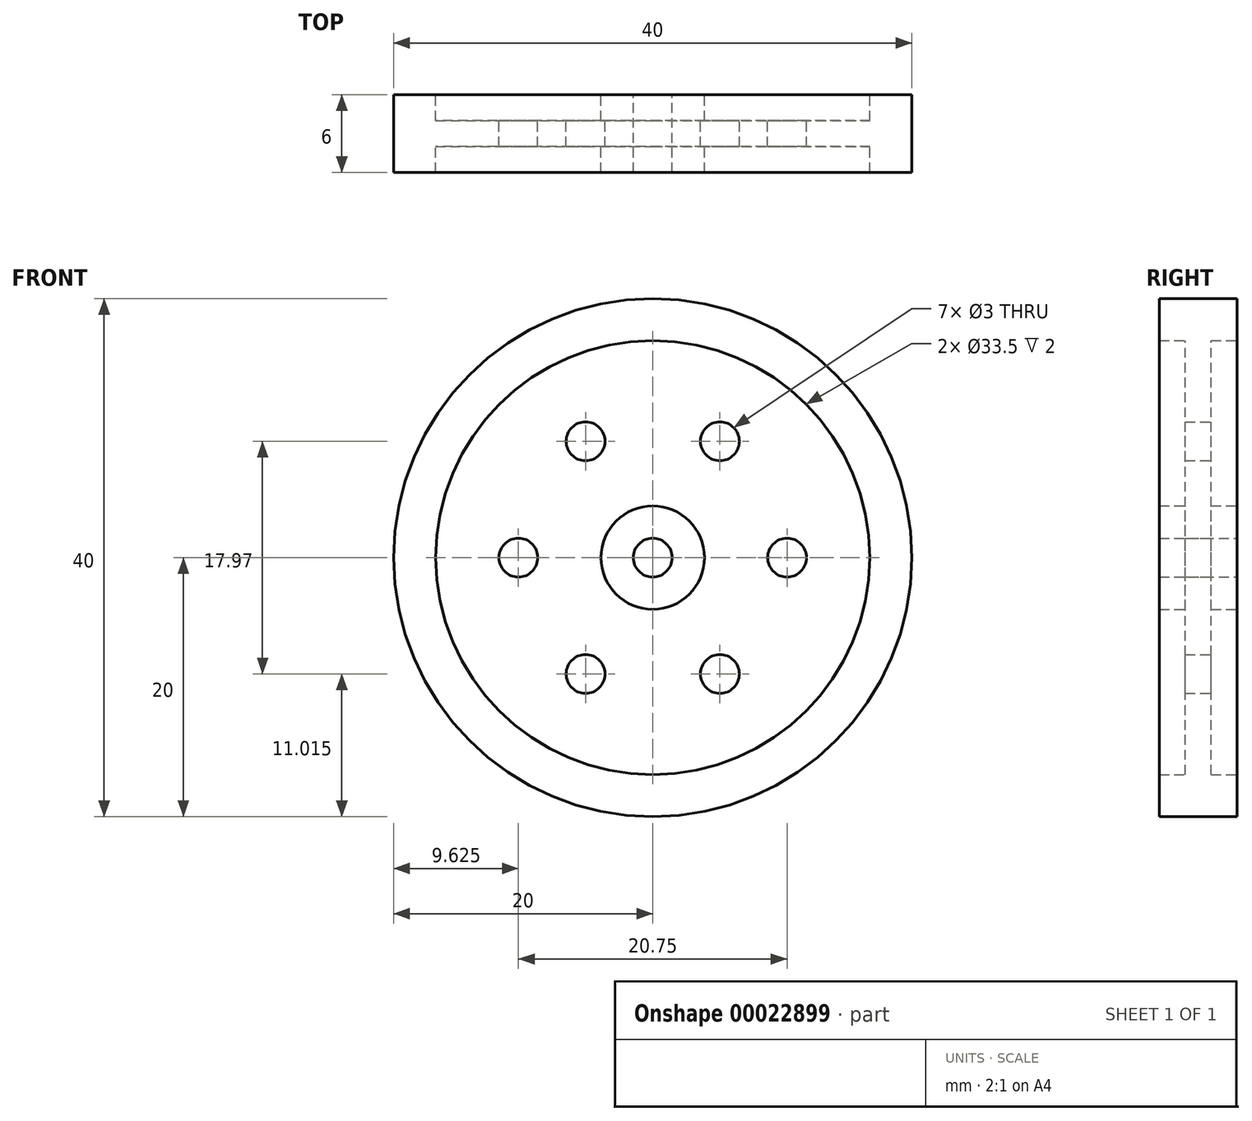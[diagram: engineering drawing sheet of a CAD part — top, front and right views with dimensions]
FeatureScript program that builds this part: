
annotation { "Feature Type Name" : "Feature", "Feature Type Description" : "" }
export const myFeature = defineFeature(function(context is Context, id is Id, definition is map)
    precondition{}
    {
        {
            var Q0;
            Q0=qCreatedBy(makeId("Front.planeOp"),FACE);
            var sketch = newSketch(context, id + "F0", { "sketchPlane" : qUnion([Q0])});
            skCircle(sketch, "E0", {"center": v(0, 0) * mm, "radius": 20 * mm});
            skCircle(sketch, "E1", {"center": v(0, 0) * mm, "radius": 16.75 * mm});
            skCircle(sketch, "E2", {"center": v(0, 0) * mm, "radius": 4 * mm});
            skCircle(sketch, "E3", {"center": v(0, 0) * mm, "radius": 1.5 * mm});
            skCircle(sketch, "E4", {"center": v(-10.38, 0) * mm, "radius": 1.5 * mm});
            skCircle(sketch, "E5.1.0", {"center": v(-5.19, -8.99) * mm, "radius": 1.5 * mm});
            skCircle(sketch, "E5.2.0", {"center": v(5.19, -8.99) * mm, "radius": 1.5 * mm});
            skCircle(sketch, "E5.3.0", {"center": v(10.38, 0) * mm, "radius": 1.5 * mm});
            skCircle(sketch, "E5.4.0", {"center": v(5.19, 8.99) * mm, "radius": 1.5 * mm});
            skCircle(sketch, "E5.5.0", {"center": v(-5.19, 8.99) * mm, "radius": 1.5 * mm});
            skSolve(sketch);
        }
        {
            var Q0;
            Q0=makeQuery(id+"F0.imprint","IMPRINT",FACE,{"disambiguationData":[TD([[makeQuery(id+"F0.imprint","IMPRINT",EDGE,{"derivedFrom":sQuery(id+"F0.wireOp",EDGE,"E1")}),1.0]])]});
            extrude(context, id + "F1", {"entities" : qUnion([Q0]), "endBound" : BoundingType.SYMMETRIC, "depth" : 2 * mm});
        }
        {
            var Q0;
            Q0=makeQuery(id+"F0.imprint","IMPRINT",FACE,{"disambiguationData":[TD([[makeQuery(id+"F0.imprint","IMPRINT",EDGE,{"derivedFrom":sQuery(id+"F0.wireOp",EDGE,"E0")}),1.0]])]});
            var Q1;
            Q1=makeQuery(id+"F0.imprint","IMPRINT",FACE,{"disambiguationData":[TD([[makeQuery(id+"F0.imprint","IMPRINT",EDGE,{"derivedFrom":sQuery(id+"F0.wireOp",EDGE,"E2")}),1.0]])]});
            extrude(context, id + "F2", {"entities" : qUnion([Q0, Q1]), "operationType" : NewBodyOperationType.ADD, "endBound" : BoundingType.SYMMETRIC, "depth" : 6 * mm});
        }
    });
